FCSTD DOCUMENT  (FreeCAD 1.0R39109 (Git))
Label: GcodeExample
License: All rights reserved
LicenseURL: https://en.wikipedia.org/wiki/All_rights_reserved
objects: Part::Part2DObjectPython×22
note: 22 computed .brp shape members not serialized (recipe doc carries the construction recipe); baked Part::Feature solids carry a one-line shape summary decoded from their .brp

FEATURE [Part::Part2DObjectPython] Line  # Draft 2D object (typed FeaturePython)
  Area = 0
  ChamferSize = 0
  Closed = false
  End = (0,10,0)
  FilletRadius = 0
  Length = 10
  MakeFace = true
  Points = (2) [(0,0,0),(0,10,0)]
  Start = (0,0,0)
  Subdivisions = 0
FEATURE [Part::Part2DObjectPython] Line001  # Draft 2D object (typed FeaturePython)
  Area = 0
  ChamferSize = 0
  Closed = false
  End = (7,5,0)
  FilletRadius = 0
  Length = 7
  MakeFace = true
  Placement = pos=(0,5,0) rot=(0,0,1;0rad)
  Points = (2) [(0,0,0),(7,0,0)]
  Start = (0,5,0)
  Subdivisions = 0
FEATURE [Part::Part2DObjectPython] Line002  # Draft 2D object (typed FeaturePython)
  Area = 0
  ChamferSize = 0
  Closed = false
  End = (7,10,0)
  FilletRadius = 0
  Length = 10
  MakeFace = true
  Placement = pos=(7,0,0) rot=(0,0,1;0rad)
  Points = (2) [(0,0,0),(0,10,0)]
  Start = (7,0,0)
  Subdivisions = 0
FEATURE [Part::Part2DObjectPython] Line003  # Draft 2D object (typed FeaturePython)
  Area = 0
  ChamferSize = 0
  Closed = false
  End = (16,2.5,0)
  FilletRadius = 0
  Length = 5
  MakeFace = true
  Placement = pos=(11,2.5,0) rot=(0,0,1;0rad)
  Points = (2) [(0,0,0),(5,0,0)]
  Start = (11,2.5,0)
  Subdivisions = 0
FEATURE [Part::Part2DObjectPython] Arc  # Draft 2D object (typed FeaturePython)
  Area = 0
  FirstAngle = 0
  LastAngle = 270
  MakeFace = true
  Placement = pos=(13.5,2.5,0) rot=(0,0,1;0rad)
  Radius = 2.5
FEATURE [Part::Part2DObjectPython] Line004  # Draft 2D object (typed FeaturePython)
  Area = 0
  ChamferSize = 0
  Closed = false
  End = (16,0,0)
  FilletRadius = 0
  Length = 2.5
  MakeFace = true
  Placement = pos=(13.5,0,0) rot=(0,0,1;0rad)
  Points = (2) [(0,0,0),(2.5,0,0)]
  Start = (13.5,0,0)
  Subdivisions = 0
FEATURE [Part::Part2DObjectPython] Line005  # Draft 2D object (typed FeaturePython)
  Area = 0
  ChamferSize = 0
  Closed = false
  End = (20,9,0)
  FilletRadius = 0
  Length = 9
  MakeFace = true
  Placement = pos=(20,0,0) rot=(0,0,1;0rad)
  Points = (2) [(0,0,0),(0,9,0)]
  Start = (20,0,0)
  Subdivisions = 0
FEATURE [Part::Part2DObjectPython] Line006  # Draft 2D object (typed FeaturePython)
  Area = 0
  ChamferSize = 0
  Closed = false
  End = (26,0,0)
  FilletRadius = 0
  Length = 9
  MakeFace = true
  Placement = pos=(26,9,0) rot=(0,0,1;0rad)
  Points = (2) [(0,0,0),(0,-9,0)]
  Start = (26,9,0)
  Subdivisions = 0
FEATURE [Part::Part2DObjectPython] Circle  # Draft 2D object (typed FeaturePython)
  Area = 0
  FirstAngle = 0
  LastAngle = 0
  MakeFace = false
  Placement = pos=(32.5,2.5,0) rot=(0,0,1;0rad)
  Radius = 2.5
FEATURE [Part::Part2DObjectPython] Line007  # Draft 2D object (typed FeaturePython)
  Area = 0
  ChamferSize = 0
  Closed = false
  End = (47,0,0)
  FilletRadius = 0
  Length = 5.38516
  MakeFace = false
  Placement = pos=(45,5,0) rot=(0,0,1;0rad)
  Points = (2) [(0,0,0),(2,-5,0)]
  Start = (45,5,0)
  Subdivisions = 0
FEATURE [Part::Part2DObjectPython] Line008  # Draft 2D object (typed FeaturePython)
  Area = 0
  ChamferSize = 0
  Closed = false
  End = (48.5,3,0)
  FilletRadius = 0
  Length = 3.3541
  MakeFace = false
  Placement = pos=(47,0,0) rot=(0,0,1;0rad)
  Points = (2) [(0,0,0),(1.5,3,0)]
  Start = (47,0,0)
  Subdivisions = 0
FEATURE [Part::Part2DObjectPython] Line009  # Draft 2D object (typed FeaturePython)
  Area = 0
  ChamferSize = 0
  Closed = false
  End = (50,0,0)
  FilletRadius = 0
  Length = 3.3541
  MakeFace = false
  Placement = pos=(48.5,3,0) rot=(0,0,1;0rad)
  Points = (2) [(0,0,0),(1.5,-3,0)]
  Start = (48.5,3,0)
  Subdivisions = 0
FEATURE [Part::Part2DObjectPython] Line010  # Draft 2D object (typed FeaturePython)
  Area = 0
  ChamferSize = 0
  Closed = false
  End = (52.5,5,0)
  FilletRadius = 0
  Length = 5.59017
  MakeFace = false
  Placement = pos=(50,0,0) rot=(0,0,1;0rad)
  Points = (2) [(0,0,0),(2.5,5,0)]
  Start = (50,0,0)
  Subdivisions = 0
FEATURE [Part::Part2DObjectPython] Circle001  # Draft 2D object (typed FeaturePython)
  Area = 0
  FirstAngle = 0
  LastAngle = 0
  MakeFace = false
  Placement = pos=(57.5,2.5,0) rot=(0,0,1;0rad)
  Radius = 2.5
FEATURE [Part::Part2DObjectPython] Line011  # Draft 2D object (typed FeaturePython)
  Area = 0
  ChamferSize = 0
  Closed = false
  End = (64,5,0)
  FilletRadius = 0
  Length = 5
  MakeFace = false
  Placement = pos=(64,0,0) rot=(0,0,1;0rad)
  Points = (2) [(0,0,0),(0,5,0)]
  Start = (64,0,0)
  Subdivisions = 0
FEATURE [Part::Part2DObjectPython] Line012  # Draft 2D object (typed FeaturePython)
  Area = 0
  ChamferSize = 0
  Closed = false
  End = (64,4,0)
  FilletRadius = 0
  Length = 1
  MakeFace = false
  Placement = pos=(64,5,0) rot=(0,0,1;0rad)
  Points = (2) [(0,0,0),(0,-1,0)]
  Start = (64,5,0)
  Subdivisions = 0
FEATURE [Part::Part2DObjectPython] Arc001  # Draft 2D object (typed FeaturePython)
  Area = 0
  FirstAngle = 0
  LastAngle = 77.5683
  MakeFace = false
  Placement = pos=(66.5,0.888864,0) rot=(0.432211,0.901773,0;3.14159rad)
  Radius = 3.99114
FEATURE [Part::Part2DObjectPython] Line013  # Draft 2D object (typed FeaturePython)
  Area = 0
  ChamferSize = 0
  Closed = false
  End = (73,9,0)
  FilletRadius = 0
  Length = 9
  MakeFace = false
  Placement = pos=(73,0,0) rot=(0,0,1;0rad)
  Points = (2) [(0,0,0),(0,9,0)]
  Start = (73,0,0)
  Subdivisions = 0
FEATURE [Part::Part2DObjectPython] Line014  # Draft 2D object (typed FeaturePython)
  Area = 0
  ChamferSize = 0
  Closed = false
  End = (81,0,0)
  FilletRadius = 0
  Length = 9
  MakeFace = false
  Placement = pos=(81,9,0) rot=(0,0,1;0rad)
  Points = (2) [(0,0,0),(0,-9,0)]
  Start = (81,9,0)
  Subdivisions = 0
FEATURE [Part::Part2DObjectPython] Line015  # Draft 2D object (typed FeaturePython)
  Area = 0
  ChamferSize = 0
  Closed = false
  End = (79.5,0,0)
  FilletRadius = 0
  Length = 1.5
  MakeFace = false
  Placement = pos=(81,0,0) rot=(0,0,1;0rad)
  Points = (2) [(0,0,0),(-1.5,0,0)]
  Start = (81,0,0)
  Subdivisions = 0
FEATURE [Part::Part2DObjectPython] Arc002  # Draft 2D object (typed FeaturePython)
  Area = 0
  FirstAngle = 90
  LastAngle = 270
  MakeFace = false
  Placement = pos=(79.5,2.5,0) rot=(0,0,1;0rad)
  Radius = 2.5
FEATURE [Part::Part2DObjectPython] Line016  # Draft 2D object (typed FeaturePython)
  Area = 0
  ChamferSize = 0
  Closed = false
  End = (81,5,0)
  FilletRadius = 0
  Length = 1.5
  MakeFace = false
  Placement = pos=(79.5,5,0) rot=(0,0,1;0rad)
  Points = (2) [(0,0,0),(1.5,0,0)]
  Start = (79.5,5,0)
  Subdivisions = 0
